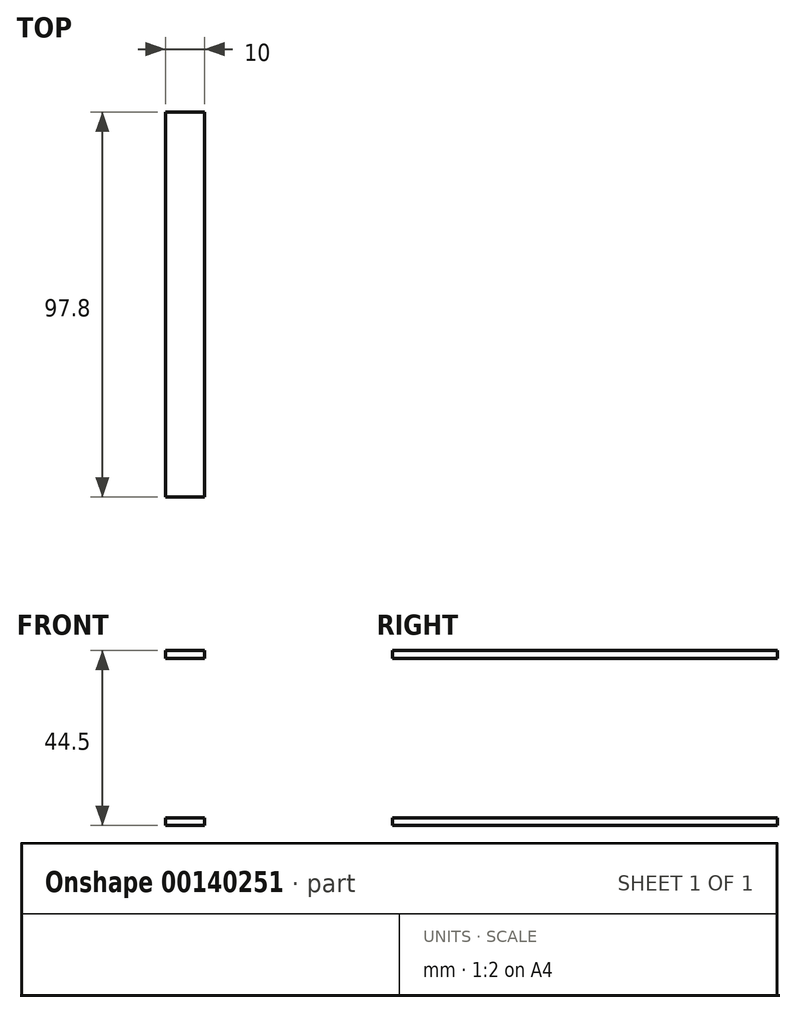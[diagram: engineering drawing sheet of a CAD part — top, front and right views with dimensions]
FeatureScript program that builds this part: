
annotation { "Feature Type Name" : "Feature", "Feature Type Description" : "" }
export const myFeature = defineFeature(function(context is Context, id is Id, definition is map)
    precondition{}
    {
        {
            var Q0;
            Q0=qCreatedBy(makeId("Right.planeOp"),FACE);
            var sketch = newSketch(context, id + "F0", { "sketchPlane" : qUnion([Q0])});
            skLineSegment(sketch, "E0.bottom", {"start": v(14.8, 20.62) * mm, "end": v(-61.4, 20.62) * mm});
            skLineSegment(sketch, "E0.top", {"start": v(14.8, -23.88) * mm, "end": v(-61.4, -23.88) * mm});
            skLineSegment(sketch, "E0.right", {"start": v(-61.4, 20.62) * mm, "end": v(-61.4, -23.88) * mm});
            skPoint(sketch, "E0.middle", {"position": v(-23.3, -1.63) * mm});
            skLineSegment(sketch, "E1.0", {"start": v(14.8, -21.88) * mm, "end": v(-61.4, -21.88) * mm});
            skLineSegment(sketch, "E2.0", {"start": v(14.8, 18.62) * mm, "end": v(-61.4, 18.62) * mm});
            skLineSegment(sketch, "E3.0", {"start": v(14.8, -2.38) * mm, "end": v(-61.4, -2.38) * mm});
            skLineSegment(sketch, "E4", {"start": v(-23.3, -2.38) * mm, "end": v(-1.7, -2.38) * mm});
            skCircle(sketch, "E5", {"center": v(-23.3, -2.38) * mm, "radius": 6.1 * mm});
            skCircle(sketch, "E6", {"center": v(-1.7, -2.38) * mm, "radius": 6.1 * mm});
            skLineSegment(sketch, "E7", {"start": v(-1.7, -2.38) * mm, "end": v(19.9, -2.37) * mm});
            skLineSegment(sketch, "E8", {"start": v(19.9, -2.37) * mm, "end": v(36.4, -2.37) * mm});
            skLineSegment(sketch, "E9.bottom", {"start": v(14.8, 20.62) * mm, "end": v(36.4, 20.62) * mm});
            skLineSegment(sketch, "E9.top", {"start": v(14.8, -2.37) * mm, "end": v(36.4, -2.37) * mm});
            skLineSegment(sketch, "E9.right", {"start": v(36.4, 20.62) * mm, "end": v(36.4, -2.37) * mm});
            skLineSegment(sketch, "E10.bottom", {"start": v(36.4, -2.37) * mm, "end": v(14.8, -2.37) * mm});
            skLineSegment(sketch, "E10.top", {"start": v(36.4, -23.88) * mm, "end": v(14.8, -23.88) * mm});
            skLineSegment(sketch, "E10.left", {"start": v(36.4, -2.37) * mm, "end": v(36.4, -23.88) * mm});
            skLineSegment(sketch, "E11", {"start": v(14.8, 18.62) * mm, "end": v(36.4, 18.62) * mm});
            skLineSegment(sketch, "E12", {"start": v(14.8, -21.88) * mm, "end": v(36.4, -21.87) * mm});
            skCircle(sketch, "E13", {"center": v(19.9, -2.37) * mm, "radius": 6.1 * mm});
            skLineSegment(sketch, "E14", {"start": v(-61.4, -2.38) * mm, "end": v(-44.9, -2.38) * mm});
            skCircle(sketch, "E15", {"center": v(-44.9, -2.38) * mm, "radius": 6.2 * mm});
            skLineSegment(sketch, "E16", {"start": v(-51.1, -2.38) * mm, "end": v(-56.1, -2.38) * mm});
            skArc(sketch, "E17", {"start": v(-61.4, -21.88) * mm, "mid": v(-56.1, -1.63) * mm, "end": v(-61.4, 18.62) * mm});
            skLineSegment(sketch, "E18", {"start": v(26, -2.37) * mm, "end": v(31, -2.37) * mm});
            skArc(sketch, "E19", {"start": v(36.4, 18.62) * mm, "mid": v(31, -1.63) * mm, "end": v(36.4, -21.88) * mm});
            skArc(sketch, "E20", {"start": v(-44.9, 18.63) * mm, "mid": v(-12.5, 8.73) * mm, "end": v(19.9, 18.63) * mm});
            skArc(sketch, "E21", {"start": v(19.9, -21.87) * mm, "mid": v(-12.5, -11.98) * mm, "end": v(-44.9, -21.88) * mm});
            skSolve(sketch);
        }
        {
            var Q0;
            {var subQ5=sQuery(id+"F0.wireOp",EDGE,"E0.bottom");Q0=makeQuery(id+"F0.imprint","IMPRINT",FACE,{"disambiguationData":[TD([[makeQuery(id+"F0.imprint","IMPRINT",EDGE,{"derivedFrom":subQ5}),1.0]])]});}
            var Q1;
            {var subQ3=sQuery(id+"F0.wireOp",EDGE,"E0.top");Q1=makeQuery(id+"F0.imprint","IMPRINT",FACE,{"disambiguationData":[TD([[makeQuery(id+"F0.imprint","IMPRINT",EDGE,{"derivedFrom":subQ3}),-1.0]])]});}
            var Q2;
            {var subQ0=sQuery(id+"F0.wireOp",EDGE,"E16");Q2=makeQuery(id+"F0.imprint","IMPRINT",FACE,{"disambiguationData":[TD([[makeQuery(id+"F0.imprint","IMPRINT",EDGE,{"derivedFrom":subQ0}),1.0]])]});}
            var Q3;
            {var subQ0=sQuery(id+"F0.wireOp",EDGE,"E16");Q3=makeQuery(id+"F0.imprint","IMPRINT",FACE,{"disambiguationData":[TD([[makeQuery(id+"F0.imprint","IMPRINT",EDGE,{"derivedFrom":subQ0}),-1.0]])]});}
            extrude(context, id + "F1", {"entities" : qUnion([Q0, Q1, Q2, Q3]), "endBound" : BoundingType.SYMMETRIC, "depth" : 10 * mm});
        }
    });
